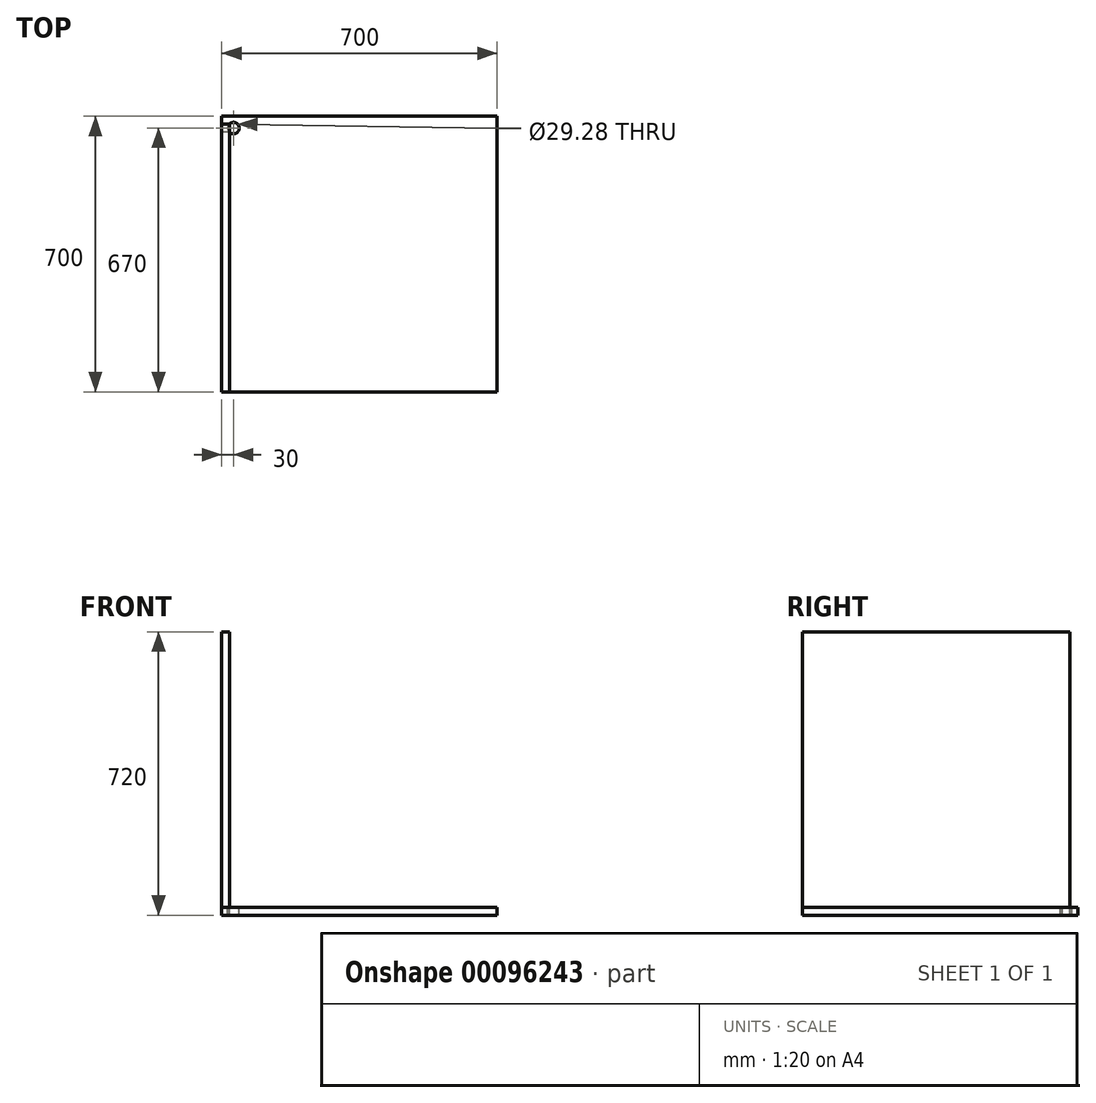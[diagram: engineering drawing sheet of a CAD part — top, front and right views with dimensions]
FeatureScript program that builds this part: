
annotation { "Feature Type Name" : "Feature", "Feature Type Description" : "" }
export const myFeature = defineFeature(function(context is Context, id is Id, definition is map)
    precondition{}
    {
        {
            assignVariable(context, id + "F0", {"name" : "thickness", "anyValue" : 20});
        }
        {
            var Q0;
            Q0=qCreatedBy(makeId("Top.planeOp"),FACE);
            var sketch = newSketch(context, id + "F1", { "sketchPlane" : qUnion([Q0])});
            skLineSegment(sketch, "E0.bottom", {"start": v(0, 0) * mm, "end": v(700, 0) * mm});
            skLineSegment(sketch, "E0.top", {"start": v(0, 700) * mm, "end": v(700, 700) * mm});
            skLineSegment(sketch, "E0.left", {"start": v(0, 0) * mm, "end": v(0, 700) * mm});
            skLineSegment(sketch, "E0.right", {"start": v(700, 0) * mm, "end": v(700, 700) * mm});
            skLineSegment(sketch, "E1", {"start": v(30, 700) * mm, "end": v(30, 670) * mm, "construction": true});
            skLineSegment(sketch, "E2", {"start": v(30, 670) * mm, "end": v(0, 670) * mm, "construction": true});
            skCircle(sketch, "E3", {"center": v(30, 670) * mm, "radius": 14.64 * mm});
            skSolve(sketch);
        }
        {
            var Q0;
            Q0=makeQuery(id+"F1.imprint","IMPRINT",FACE,{"disambiguationData":[TD([[makeQuery(id+"F1.imprint","IMPRINT",EDGE,{"derivedFrom":sQuery(id+"F1.wireOp",EDGE,"E0.bottom")}),1.0]])]});
            extrude(context, id + "F2", {"entities" : qUnion([Q0]), "oppositeDirection" : true, "depth" : (getVariable(context, 'thickness')) * mm});
        }
        {
            var Q0;
            Q0=qCreatedBy(makeId("Right.planeOp"),FACE);
            var sketch = newSketch(context, id + "F3", { "sketchPlane" : qUnion([Q0])});
            skLineSegment(sketch, "E4.bottom", {"start": v(700, 0) * mm, "end": v(0, 0) * mm});
            skLineSegment(sketch, "E4.top", {"start": v(680, 700) * mm, "end": v(0, 700) * mm});
            skLineSegment(sketch, "E4.left", {"start": v(680, 0) * mm, "end": v(680, 700) * mm});
            skLineSegment(sketch, "E4.right", {"start": v(0, 0) * mm, "end": v(0, 700) * mm});
            skLineSegment(sketch, "E5", {"start": v(670, 0) * mm, "end": v(670, -20) * mm});
            skLineSegment(sketch, "E6.bottom", {"start": v(670, -20) * mm, "end": v(680, -20) * mm});
            skLineSegment(sketch, "E6.top", {"start": v(670, 0) * mm, "end": v(680, 0) * mm});
            skLineSegment(sketch, "E6.left", {"start": v(670, -20) * mm, "end": v(670, 0) * mm});
            skLineSegment(sketch, "E6.right", {"start": v(680, -20) * mm, "end": v(680, 0) * mm});
            skLineSegment(sketch, "E7.MirrorCS", {"start": v(670, 0) * mm, "end": v(660, 0) * mm});
            skLineSegment(sketch, "E8.MirrorCS", {"start": v(660, -20) * mm, "end": v(660, 0) * mm});
            skLineSegment(sketch, "E9.MirrorCS", {"start": v(670, -20) * mm, "end": v(660, -20) * mm});
            skSolve(sketch);
        }
        {
            var Q0;
            Q0 = qSketchRegion(id + "F3", true);
            extrude(context, id + "F4", {"entities" : qUnion([Q0]), "depth" : (getVariable(context, 'thickness')) * mm});
        }
    });
